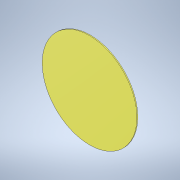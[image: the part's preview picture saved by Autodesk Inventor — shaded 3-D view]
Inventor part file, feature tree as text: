
AUTODESK INVENTOR PART (.ipt)
format: ipt  version: 2020.4 (Build 244396000, 396)  size: 94,720 bytes
history: native  units: mm
features: extrude x1, sketch x1
ambient origin geometry x8: Origin, YZ Plane, XZ Plane, XY Plane, X Axis, Y Axis, Z Axis, Center Point
bodies: Solid1 (feature_tree)
feature tree (2):
  extrude  "Extrusion1"  Depth=0.5mm TaperAngle=0.0deg
  sketch  "Sketch1"  dims[d0=52.0mm d1=0.5mm d2=0.0mm]
